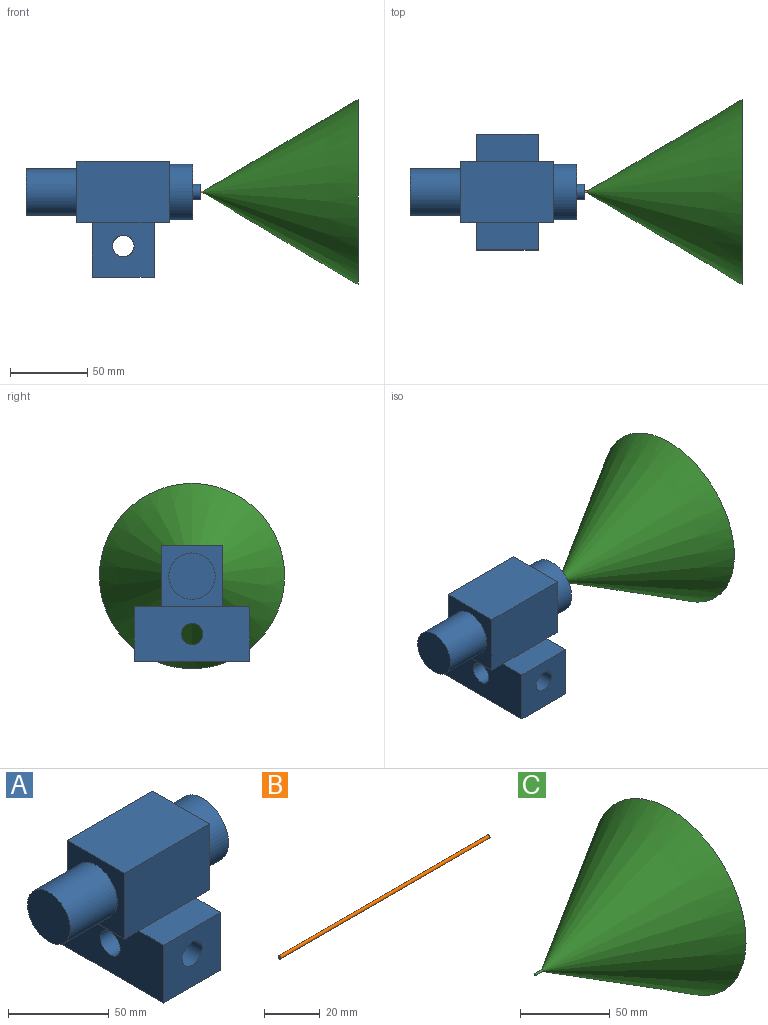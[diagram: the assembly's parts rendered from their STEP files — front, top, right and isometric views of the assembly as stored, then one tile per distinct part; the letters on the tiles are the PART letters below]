
ASSEMBLY  parts=3 mates=2
PART A: 26 faces, bbox 113x75x75 mm
  f0: cylinder r=18mm len=36mm, axis (-1,0,0), area 1696.5mm2, adj f8,f22
  f1: cylinder r=7mm len=75mm, axis (0,-1,0), area 2929mm2, adj f2,f3,f15,f17,f20
  f2: cylinder r=7mm len=19.04mm, axis (-1,0,0), area 642.7mm2, adj f1,f14,f20
  f3: cylinder r=7mm len=19.04mm, axis (-1,0,0), area 642.7mm2, adj f1,f16,f20
  f4: plane 40x10mm, normal (0,0,-1), area 400mm2, adj f8,f9,f10,f14
  f5: plane 60x40mm, normal (0,0,1), area 2400mm2, adj f6,f8,f9,f10
  f6: plane 40x40mm, normal (-1,0,0), area 893.1mm2, adj f5,f7,f9,f10,f11
  f7: plane 40x10mm, normal (0,0,-1), area 400mm2, adj f6,f9,f10,f16
  f8: plane 40x40mm, normal (1,0,0), area 582.1mm2, adj f0,f4,f5,f9,f10
  f9: plane 60x40mm, normal (0,1,0), area 2400mm2, adj f4,f5,f6,f7,f8,f13
  f10: plane 60x40mm, normal (0,-1,0), area 2400mm2, adj f4,f5,f6,f7,f8,f19
  f11: cylinder r=15mm len=33mm, axis (1,0,0), area 3110.2mm2, adj f6,f12
  f12: plane 30x30mm, normal (-1,0,0), area 706.9mm2, adj f11
  f13: plane 40x17.5mm, normal (0,0,1), area 700mm2, adj f9,f14,f16,f17
  f14: plane 75x35mm, normal (1,0,0), area 2471.1mm2, adj f2,f4,f13,f15,f17,f18,f19
  f15: plane 40x35mm, normal (0,-1,0), area 1246.1mm2, adj f1,f14,f16,f18,f19
  f16: plane 75x35mm, normal (-1,0,0), area 2471.1mm2, adj f3,f7,f13,f15,f17,f18,f19
  f17: plane 40x35mm, normal (0,1,0), area 1246.1mm2, adj f1,f13,f14,f16,f18
  f18: plane 75x40mm, normal (0,0,-1), area 2905mm2, adj f14,f15,f16,f17,f20
  f19: plane 40x17.5mm, normal (0,0,1), area 700mm2, adj f10,f14,f15,f16
  f20: cylinder r=5.5mm len=13.07mm, axis (0,0,-1), area 405.9mm2, adj f1,f2,f3,f18
  f21: cylinder r=5mm len=10mm, axis (1,0,0), area 157.1mm2, adj f22,f25
  f22: plane 36x36mm, normal (1,0,0), area 939.3mm2, adj f0,f21
  f23: cone r=0mm half-angle=59deg, axis (1,0,0), area 1.8mm2, adj f24
  f24: cylinder r=0.7mm len=6mm, axis (1,0,0), area 26.4mm2, adj f23,f25
  f25: plane 10x10mm, normal (1,0,0), area 77mm2, adj f21,f24
PART B: 3 faces, bbox 106x1.3x1.3 mm
  f0: cylinder r=0.65mm len=106mm, axis (-1,0,0), area 432.9mm2, adj f1,f2
  f1: plane 1.3x1.3mm, normal (-1,0,0), area 1.3mm2, adj f0
  f2: plane 1.3x1.3mm, normal (1,0,0), area 1.3mm2, adj f0
PART C: 5 faces, bbox 106x120x120 mm
  f0: cylinder r=0.65mm len=6mm, axis (-1,0,0), area 24.5mm2, adj f1,f3
  f1: plane 1.3x1.3mm, normal (-1,0,0), area 1.3mm2, adj f0
  f2: plane 120x120mm, normal (1,0,0), area 859.8mm2, adj f3,f4
  f3: cone r=0.65mm half-angle=30.7deg, axis (1,0,0), area 22156.8mm2, adj f0,f2
  f4: cone r=0.65mm half-angle=30.7deg, axis (1,0,0), area 20474.9mm2, adj f2
PLACE A t=(38.2,15.67,-9.57)mm
PLACE B t=(88.2,15.67,10.43)mm
PLACE C t=(90.2,15.67,10.43)mm
MATE revolute C.f0 <-> A.f0  axis (1,0,0) through (90.2,15.67,10.43)mm
MATE fastened B.f0 <-> A.f0  axis (-1,0,0) through (82.2,15.67,10.43)mm
